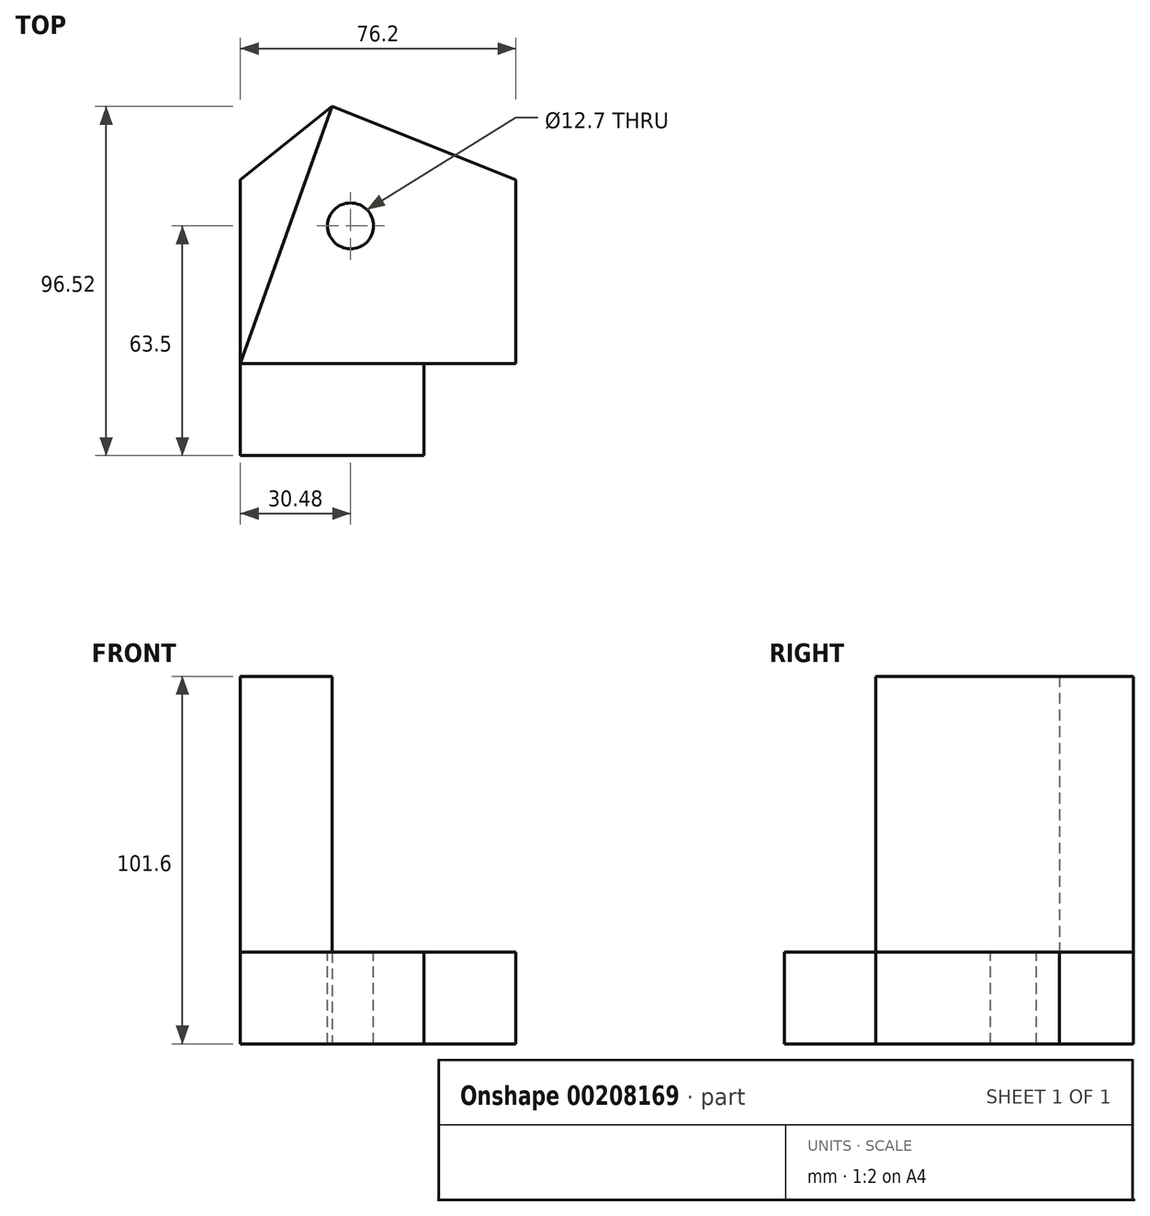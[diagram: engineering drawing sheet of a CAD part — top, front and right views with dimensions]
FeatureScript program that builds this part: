
annotation { "Feature Type Name" : "Feature", "Feature Type Description" : "" }
export const myFeature = defineFeature(function(context is Context, id is Id, definition is map)
    precondition{}
    {
        {
            var Q0;
            Q0=qCreatedBy(makeId("Top.planeOp"),FACE);
            var sketch = newSketch(context, id + "F0", { "sketchPlane" : qUnion([Q0])});
            skLineSegment(sketch, "E0.bottom", {"start": v(0, 0) * mm, "end": v(76.2, 0) * mm});
            skLineSegment(sketch, "E0.top", {"start": v(0, 50.8) * mm, "end": v(76.2, 50.8) * mm});
            skLineSegment(sketch, "E0.left", {"start": v(0, 0) * mm, "end": v(0, 50.8) * mm});
            skLineSegment(sketch, "E0.right", {"start": v(76.2, 0) * mm, "end": v(76.2, 50.8) * mm});
            skLineSegment(sketch, "E1", {"start": v(0, 50.8) * mm, "end": v(25.4, 71.12) * mm});
            skLineSegment(sketch, "E2", {"start": v(25.4, 71.12) * mm, "end": v(76.2, 50.8) * mm});
            skSolve(sketch);
        }
        {
            var Q0;
            Q0 = qSketchRegion(id + "F0", true);
            extrude(context, id + "F1", {"entities" : qUnion([Q0]), "depth" : 25.4 * mm});
        }
        {
            var Q0;
            Q0=makeQuery(id+"F1.opExtrude","SWEPT_FACE",FACE,{"disambiguationData":[OSD([sQuery(id+"F0.wireOp",EDGE,"E0.bottom")])]});
            var sketch = newSketch(context, id + "F2", { "sketchPlane" : qUnion([Q0])});
            skLineSegment(sketch, "E3.bottom", {"start": v(0, 0) * mm, "end": v(50.8, 0) * mm});
            skLineSegment(sketch, "E3.top", {"start": v(0, 25.4) * mm, "end": v(50.8, 25.4) * mm});
            skLineSegment(sketch, "E3.left", {"start": v(0, 0) * mm, "end": v(0, 25.4) * mm});
            skLineSegment(sketch, "E3.right", {"start": v(50.8, 0) * mm, "end": v(50.8, 25.4) * mm});
            skSolve(sketch);
        }
        {
            var Q0;
            Q0 = qSketchRegion(id + "F2", true);
            extrude(context, id + "F3", {"entities" : qUnion([Q0]), "depth" : 25.4 * mm});
        }
        {
            var Q0;
            Q0=makeQuery(id+"F1.opExtrude","CAP_FACE",FACE,{"disambiguationData":[OSD([sQuery(id+"F0.wireOp",EDGE,"E0.bottom"),sQuery(id+"F0.wireOp",EDGE,"E0.left"),sQuery(id+"F0.wireOp",EDGE,"E0.right"),sQuery(id+"F0.wireOp",EDGE,"E1"),sQuery(id+"F0.wireOp",EDGE,"E2")])],"isStart":false});
            var sketch = newSketch(context, id + "F4", { "sketchPlane" : qUnion([Q0])});
            skLineSegment(sketch, "E4", {"start": v(0, 0) * mm, "end": v(25.4, 71.12) * mm});
            skLineSegment(sketch, "E5", {"start": v(25.4, 71.12) * mm, "end": v(0, 50.8) * mm});
            skLineSegment(sketch, "E6", {"start": v(0, 50.8) * mm, "end": v(0, 0) * mm});
            skSolve(sketch);
        }
        {
            var Q0;
            Q0 = qSketchRegion(id + "F4", true);
            extrude(context, id + "F5", {"entities" : qUnion([Q0]), "depth" : 76.2 * mm});
        }
        {
            var Q0;
            Q0=makeQuery(id+"F1.opExtrude","CAP_FACE",FACE,{"disambiguationData":[OSD([sQuery(id+"F0.wireOp",EDGE,"E0.bottom"),sQuery(id+"F0.wireOp",EDGE,"E0.left"),sQuery(id+"F0.wireOp",EDGE,"E0.right"),sQuery(id+"F0.wireOp",EDGE,"E1"),sQuery(id+"F0.wireOp",EDGE,"E2")])],"isStart":false});
            var sketch = newSketch(context, id + "F6", { "sketchPlane" : qUnion([Q0])});
            skCircle(sketch, "E7", {"center": v(30.48, 38.1) * mm, "radius": 6.35 * mm});
            skSolve(sketch);
        }
        {
            var Q0;
            Q0 = qSketchRegion(id + "F6", true);
            extrude(context, id + "F7", {"entities" : qUnion([Q0]), "operationType" : NewBodyOperationType.REMOVE, "endBound" : BoundingType.THROUGH_ALL, "oppositeDirection" : true, "depth" : 25.4 * mm});
        }
    });
